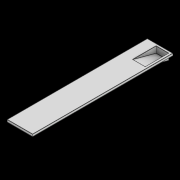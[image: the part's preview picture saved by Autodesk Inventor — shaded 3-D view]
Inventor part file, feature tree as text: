
AUTODESK INVENTOR PART (.ipt)
format: ipt  version: 2021 (Build 250183000, 183)  size: 262,656 bytes
history: native  units: mm
features: other x24, sheet_metal_op x11, sketch x11, extrude x1
ambient origin geometry x8: Origin, YZ Plane, XZ Plane, XY Plane, X Axis, Y Axis, Z Axis, Center Point
bodies: Body1 (feature_tree)
feature tree (47):
  other  "Sólido1"
  other  "Cara1"
  other  "Pestaña1"
  other  "Pestaña2"
  other  "Pestaña3"
  other  "Pestaña4"
  extrude  "Extrusión1"  Depth=6600.0mm
  sheet_metal_op  "Flange11"
  sheet_metal_op  "Flange12"
  sheet_metal_op  "Bend14"
  sheet_metal_op  "Flange13"
  sketch  "Boceto1"  dims[d0=1200.0mm d1=6600.0mm]
  other  "Placa1"
  sketch  "Boceto2"  dims[d2=4.572mm]
  other  "Placa2"
  other  "Doblez1"
  other  "Esquina1"
  sketch  "Boceto3"  dims[d3=4.572mm]
  other  "Placa3"
  other  "Doblez2"
  other  "Esquina2"
  sketch  "Boceto4"  dims[d4=2.286mm]
  other  "Placa4"
  other  "Doblez3"
  other  "Esquina3"
  sketch  "Boceto5"  dims[d5=9.144mm]
  other  "Placa5"
  other  "Doblez4"
  other  "Esquina4"
  sketch  "Boceto6"  dims[d6=4.572mm]
  sketch  "Sketch14"  dims[d7=100.0mm d8=90.0deg d9=4.572mm]
  other  "Plate13"
  sheet_metal_op  "Bend12"
  sheet_metal_op  "Corner11"
  sketch  "Sketch15"  dims[d10=18.288mm]
  other  "Plate14"
  sheet_metal_op  "Bend13"
  sheet_metal_op  "Corner12"
  sketch  "Sketch16"  dims[d11=4.572mm]
  other  "Plate15"
  sheet_metal_op  "Bend15"
  sheet_metal_op  "Corner13"
  sketch  "Sketch18"  dims[d12=4.572mm]
  sketch  "Sketch19"  dims[d13=4.572mm d14=2.286mm d15=9.144mm d16=4.572mm d17=100.0mm d18=90.0deg d19=4.572mm d20=18.288mm d21=4.572mm d22=4.572mm d23=4.572mm d24=2.286mm d25=9.144mm d26=4.572mm d27=100.0mm d28=90.0deg d29=4.572mm d30=18.288mm d31=4.572mm d32=4.572mm d33=4.572mm d34=2.286mm d35=9.144mm d36=4.572mm d37=100.0mm d38=90.0deg d39=4.572mm d40=18.288mm d41=4.572mm d42=4.572mm d43=600.0mm d44=1100.0mm d45=0.0mm d46=0.0mm d114=13.716mm d115=2.286mm d116=9.144mm d117=4.572mm d118=300.0mm d119=-15.707963mm d120=4.572mm d121=18.288mm d122=4.572mm d123=4.572mm d124=13.716mm d125=2.286mm d126=9.144mm d127=4.572mm d128=1130.0mm d129=15.0deg d130=4.572mm d131=0.0mm d132=18.288mm d133=4.572mm d134=4.572mm d135=18.288mm d136=4.572mm d137=4.572mm d138=0.0mm d139=10.0mm d140=4.572mm d141=2.286mm d142=9.144mm d143=4.572mm d144=4.572mm d145=4.572mm d146=2.286mm d147=9.144mm d148=4.572mm d149=500.0mm d150=90.0deg d151=4.572mm d152=0.0mm d153=18.288mm d154=4.572mm d155=4.572mm d156=4.572mm d157=0.0mm d158=4.572mm d159=0.0mm]
  sheet_metal_op  "Corner1"
  other  "Cut1"
  other  "Cut2"
